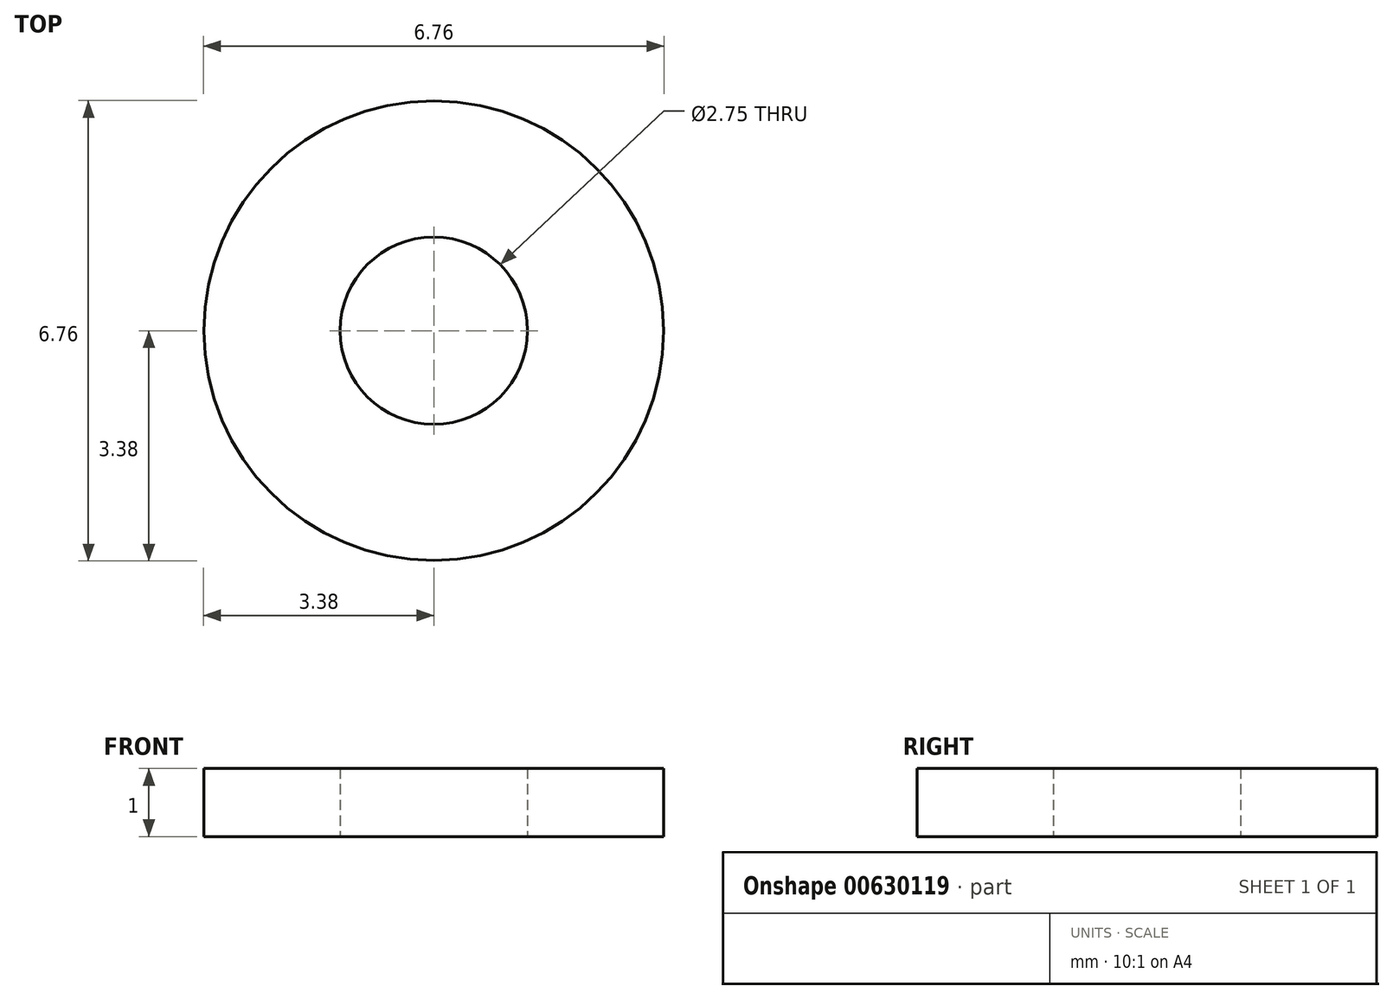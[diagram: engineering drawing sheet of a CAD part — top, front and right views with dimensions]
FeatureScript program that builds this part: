
annotation { "Feature Type Name" : "Feature", "Feature Type Description" : "" }
export const myFeature = defineFeature(function(context is Context, id is Id, definition is map)
    precondition{}
    {
        {
            var Q0;
            Q0=qCreatedBy(makeId("Top.planeOp"),FACE);
            var sketch = newSketch(context, id + "F0", { "sketchPlane" : qUnion([Q0])});
            skCircle(sketch, "E0", {"center": v(0, 0) * mm, "radius": 1.38 * mm});
            skCircle(sketch, "E1.0", {"center": v(0, 0) * mm, "radius": 3.38 * mm});
            skSolve(sketch);
        }
        {
            var Q0;
            Q0 = qSketchRegion(id + "F0", true);
            extrude(context, id + "F1", {"entities" : qUnion([Q0]), "depth" : 1 * mm, "offsetDistance" : 25 * mm});
        }
    });
